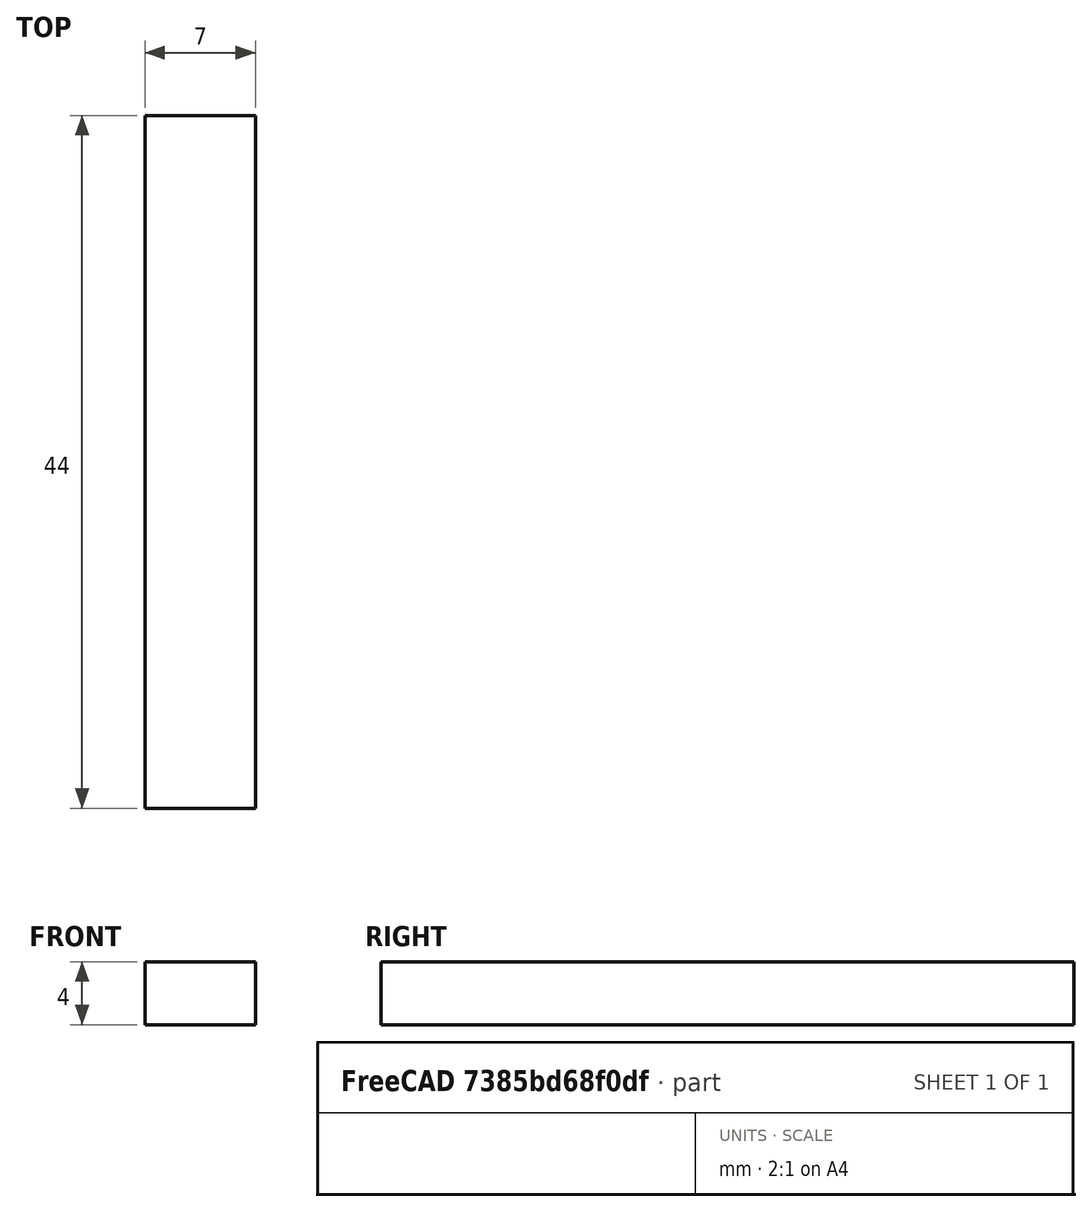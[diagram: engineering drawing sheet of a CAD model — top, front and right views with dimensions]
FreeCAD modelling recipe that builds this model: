
FCSTD DOCUMENT  (FreeCAD 0.21R33771 (Git))
Label: battery mk 1
License: All rights reserved
LicenseURL: https://en.wikipedia.org/wiki/All_rights_reserved
objects: Sketcher::SketchObject×2, PartDesign::Body×2, Mesh::Feature×1, PartDesign::Pad×1, App::Part×1
note: 6 computed .brp shape members not serialized (recipe doc carries the construction recipe); baked Part::Feature solids carry a one-line shape summary decoded from their .brp

FEATURE [Mesh::Feature] __Batterie_2_0  label="2_Batterie_2.0"
FEATURE [Sketcher::SketchObject] Sketch
  FullyConstrained = false
  MapMode = 5
  Placement = pos=(0,0,0) rot=(0.57735,0.57735,0.57735;2.0944rad)
  Support = -> [YZ_Plane]
  sketch-geometry (4):
    g0: LineSegment StartX=0 StartY=19.9801 StartZ=0 EndX=44 EndY=19.9801 EndZ=0
    g1: LineSegment StartX=44 StartY=19.9801 StartZ=0 EndX=44 EndY=15.9801 EndZ=0
    g2: LineSegment StartX=44 StartY=15.9801 StartZ=0 EndX=0 EndY=15.9801 EndZ=0
    g3: LineSegment StartX=0 StartY=15.9801 StartZ=0 EndX=0 EndY=19.9801 EndZ=0
  constraints (11):
    c: Coincident(g0,g1)
    c: Coincident(g1,g2)
    c: Coincident(g2,g3)
    c: Coincident(g3,g0)
    c: Horizontal(g0)
    c: Horizontal(g2)
    c: Vertical(g1)
    c: Vertical(g3)
    c: PointOnObject(g0,g-2)
    c: DistanceX(g0,g0) = 44
    c: DistanceY(g1,g1) = 4
FEATURE [PartDesign::Pad] Pad
  Direction = (1,-2e-16,3e-16)
  Length = 7
  Length2 = 10
  Placement = pos=(0,0,0) rot=(1,1,1;2.0944rad)
  Profile = -> Sketch
  ReferenceAxis = -> Sketch [N_Axis]
  Type = 0
FEATURE [PartDesign::Body] Body  label="screw pot"
  Group = -> [Sketch,Pad]
  Origin = -> Origin
  Placement = pos=(79.5,0,0) rot=(0,0,1;0rad)
  Tip = -> Pad
FEATURE [Sketcher::SketchObject] Sketch001
  FullyConstrained = true
  MapMode = 5
  Placement = pos=(0,0,0) rot=(0.57735,0.57735,0.57735;2.0944rad)
  Support = -> [YZ_Plane002]
FEATURE [PartDesign::Body] Body001  label="Body"
  Group = -> [Sketch001]
  Origin = -> Origin002
FEATURE [App::Part] Part
  Group = -> [Body001]
  Origin = -> Origin001
  Placement = pos=(87,0,0) rot=(0,0,1;0rad)
